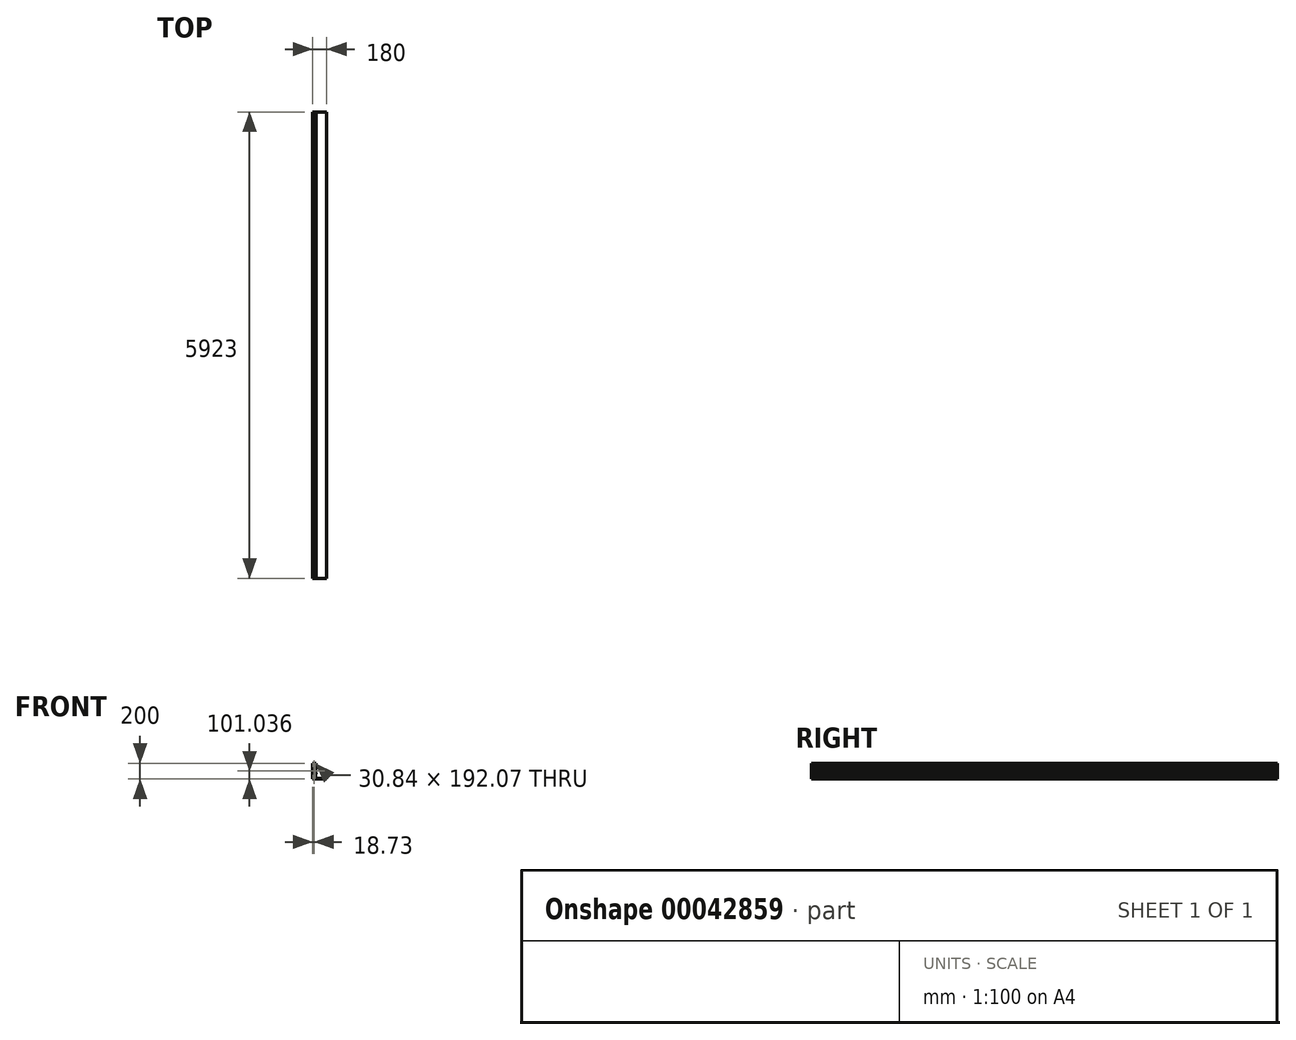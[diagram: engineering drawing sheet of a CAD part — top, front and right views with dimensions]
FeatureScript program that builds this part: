
annotation { "Feature Type Name" : "Feature", "Feature Type Description" : "" }
export const myFeature = defineFeature(function(context is Context, id is Id, definition is map)
    precondition{}
    {
        {
            var Q0;
            Q0=qCreatedBy(makeId("Front.planeOp"),FACE);
            var sketch = newSketch(context, id + "F0", { "sketchPlane" : qUnion([Q0])});
            skLineSegment(sketch, "E0", {"start": v(-175, 135) * mm, "end": v(-175, -65) * mm});
            skLineSegment(sketch, "E1", {"start": v(-175, -65) * mm, "end": v(5, -65) * mm});
            skLineSegment(sketch, "E2", {"start": v(5, -65) * mm, "end": v(5, -30) * mm});
            skLineSegment(sketch, "E3", {"start": v(5, -30) * mm, "end": v(0, -30) * mm});
            skLineSegment(sketch, "E4", {"start": v(0, -30) * mm, "end": v(0, -60) * mm});
            skLineSegment(sketch, "E5", {"start": v(0, -60) * mm, "end": v(-137, -60) * mm});
            skLineSegment(sketch, "E6", {"start": v(-137, -60) * mm, "end": v(-137, 0) * mm});
            skLineSegment(sketch, "E7", {"start": v(-175, 135) * mm, "end": v(-134, 135) * mm});
            skLineSegment(sketch, "E8", {"start": v(-134, 135) * mm, "end": v(-134, 120) * mm});
            skLineSegment(sketch, "E9", {"start": v(-134, 120) * mm, "end": v(-137, 120) * mm});
            skLineSegment(sketch, "E10", {"start": v(-137, 120) * mm, "end": v(-137, 105) * mm});
            skLineSegment(sketch, "E11", {"start": v(-137, 105) * mm, "end": v(-134, 105) * mm});
            skLineSegment(sketch, "E12", {"start": v(-134, 105) * mm, "end": v(-134, 90) * mm});
            skLineSegment(sketch, "E13", {"start": v(-134, 90) * mm, "end": v(-137, 90) * mm});
            skLineSegment(sketch, "E14", {"start": v(-137, 90) * mm, "end": v(-137, 75) * mm});
            skLineSegment(sketch, "E15", {"start": v(-137, 75) * mm, "end": v(-134, 75) * mm});
            skLineSegment(sketch, "E16", {"start": v(-134, 75) * mm, "end": v(-134, 60) * mm});
            skLineSegment(sketch, "E17", {"start": v(-134, 60) * mm, "end": v(-137, 60) * mm});
            skLineSegment(sketch, "E18", {"start": v(-137, 60) * mm, "end": v(-137, 45) * mm});
            skLineSegment(sketch, "E19", {"start": v(-137, 45) * mm, "end": v(-134, 45) * mm});
            skLineSegment(sketch, "E20", {"start": v(-134, 45) * mm, "end": v(-134, 30) * mm});
            skLineSegment(sketch, "E21", {"start": v(-134, 30) * mm, "end": v(-137, 30) * mm});
            skLineSegment(sketch, "E22", {"start": v(-137, 30) * mm, "end": v(-137, 15) * mm});
            skLineSegment(sketch, "E23", {"start": v(-137, 15) * mm, "end": v(-134, 15) * mm});
            skLineSegment(sketch, "E24", {"start": v(-134, 15) * mm, "end": v(-134, 0) * mm});
            skLineSegment(sketch, "E25", {"start": v(-134, 0) * mm, "end": v(-137, 0) * mm});
            skLineSegment(sketch, "E26.bottom", {"start": v(-171.7, 132.07) * mm, "end": v(-140.85, 132.07) * mm});
            skLineSegment(sketch, "E26.top", {"start": v(-171.7, -60) * mm, "end": v(-140.85, -60) * mm});
            skLineSegment(sketch, "E26.left", {"start": v(-171.7, 132.07) * mm, "end": v(-171.7, -60) * mm});
            skLineSegment(sketch, "E26.right", {"start": v(-140.85, 132.07) * mm, "end": v(-140.85, -60) * mm});
            skSolve(sketch);
        }
        {
            var Q0;
            Q0=makeQuery(id+"F0.imprint","IMPRINT",FACE,{"disambiguationData":[TD([[makeQuery(id+"F0.imprint","IMPRINT",EDGE,{"derivedFrom":sQuery(id+"F0.wireOp",EDGE,"E0")}),1.0]])]});
            extrude(context, id + "F1", {"entities" : qUnion([Q0]), "depth" : 5923 * mm});
        }
    });
